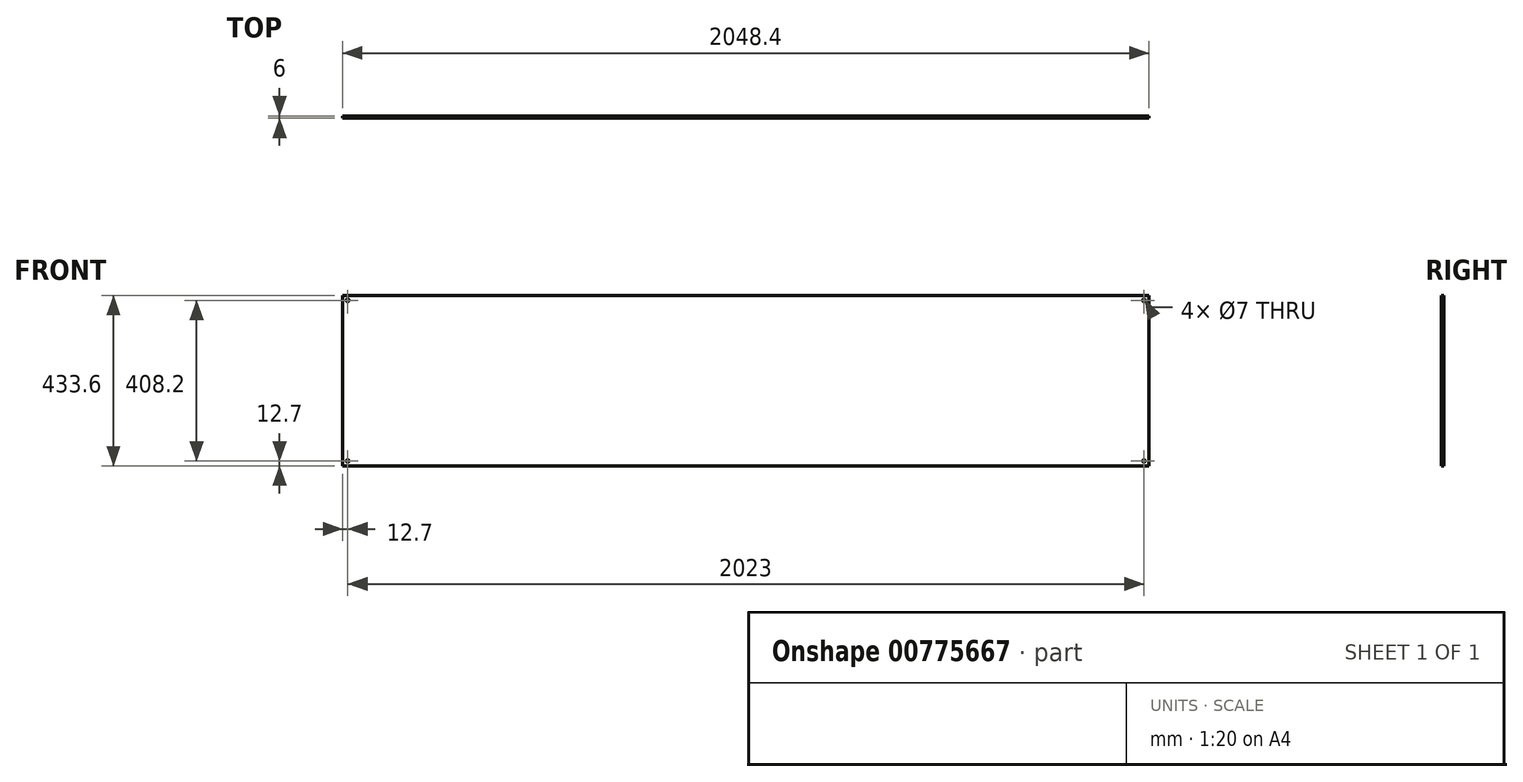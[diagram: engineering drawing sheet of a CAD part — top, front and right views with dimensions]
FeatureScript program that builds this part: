
annotation { "Feature Type Name" : "Feature", "Feature Type Description" : "" }
export const myFeature = defineFeature(function(context is Context, id is Id, definition is map)
    precondition{}
    {
        {
            var Q0;
            Q0=qCreatedBy(makeId("Front.planeOp"),FACE);
            var sketch = newSketch(context, id + "F0", { "sketchPlane" : qUnion([Q0])});
            skLineSegment(sketch, "E0.bottom", {"start": v(1024.2, -216.8) * mm, "end": v(-1024.2, -216.8) * mm});
            skLineSegment(sketch, "E0.top", {"start": v(1024.2, 216.8) * mm, "end": v(-1024.2, 216.8) * mm});
            skLineSegment(sketch, "E0.left", {"start": v(1024.2, -216.8) * mm, "end": v(1024.2, 216.8) * mm});
            skLineSegment(sketch, "E0.right", {"start": v(-1024.2, -216.8) * mm, "end": v(-1024.2, 216.8) * mm});
            skPoint(sketch, "E0.middle", {"position": v(0, 0) * mm});
            skSolve(sketch);
        }
        {
            var Q0;
            Q0=makeQuery(id+"F0.imprint","IMPRINT",FACE,{"disambiguationData":[TD([[makeQuery(id+"F0.imprint","IMPRINT",EDGE,{"derivedFrom":sQuery(id+"F0.wireOp",EDGE,"E0.bottom")}),-1.0]])]});
            extrude(context, id + "F1", {"entities" : qUnion([Q0]), "depth" : 6 * mm, "offsetDistance" : 25 * mm});
        }
        {
            var Q0;
            Q0=makeQuery(id+"F1.opExtrude","CAP_FACE",FACE,{"disambiguationData":[OSD([sQuery(id+"F0.wireOp",EDGE,"E0.bottom"),sQuery(id+"F0.wireOp",EDGE,"E0.top"),sQuery(id+"F0.wireOp",EDGE,"E0.left"),sQuery(id+"F0.wireOp",EDGE,"E0.right")])],"isStart":true});
            var sketch = newSketch(context, id + "F2", { "sketchPlane" : qUnion([Q0])});
            skPoint(sketch, "E1", {"position": v(1011.5, 204.1) * mm});
            skPoint(sketch, "E2", {"position": v(1011.5, -204.1) * mm});
            skPoint(sketch, "E3", {"position": v(-1011.5, -204.1) * mm});
            skPoint(sketch, "E4", {"position": v(-1011.5, 204.1) * mm});
            skSolve(sketch);
        }
        {
            var Q0;
            Q0=sQuery(id+"F2.wireOp",VERTEX,"E1");
            var Q1;
            Q1=sQuery(id+"F2.wireOp",VERTEX,"E2");
            var Q2;
            Q2=sQuery(id+"F2.wireOp",VERTEX,"E4");
            var Q3;
            Q3=sQuery(id+"F2.wireOp",VERTEX,"E3");
            var Q4;
            Q4=makeQuery(id+"F1.opExtrude","SWEPT_BODY",BODY,{"disambiguationData":[OSD([sQuery(id+"F0.wireOp",EDGE,"E0.bottom"),sQuery(id+"F0.wireOp",EDGE,"E0.top"),sQuery(id+"F0.wireOp",EDGE,"E0.left"),sQuery(id+"F0.wireOp",EDGE,"E0.right")])]});
            hole(context, id + "F3", {"style" : HoleStyle.SIMPLE, "endStyle" : HoleEndStyle.BLIND, "holeDiameter" : 7 * mm, "majorDiameter" : 5 * mm, "holeDepth" : 100 * mm, "isTappedThrough" : true, "tappedDepth" : 12 * mm, "tapClearance" : 3, "locations" : qUnion([Q0, Q1, Q2, Q3]), "scope" : qUnion([Q4])});
        }
    });
